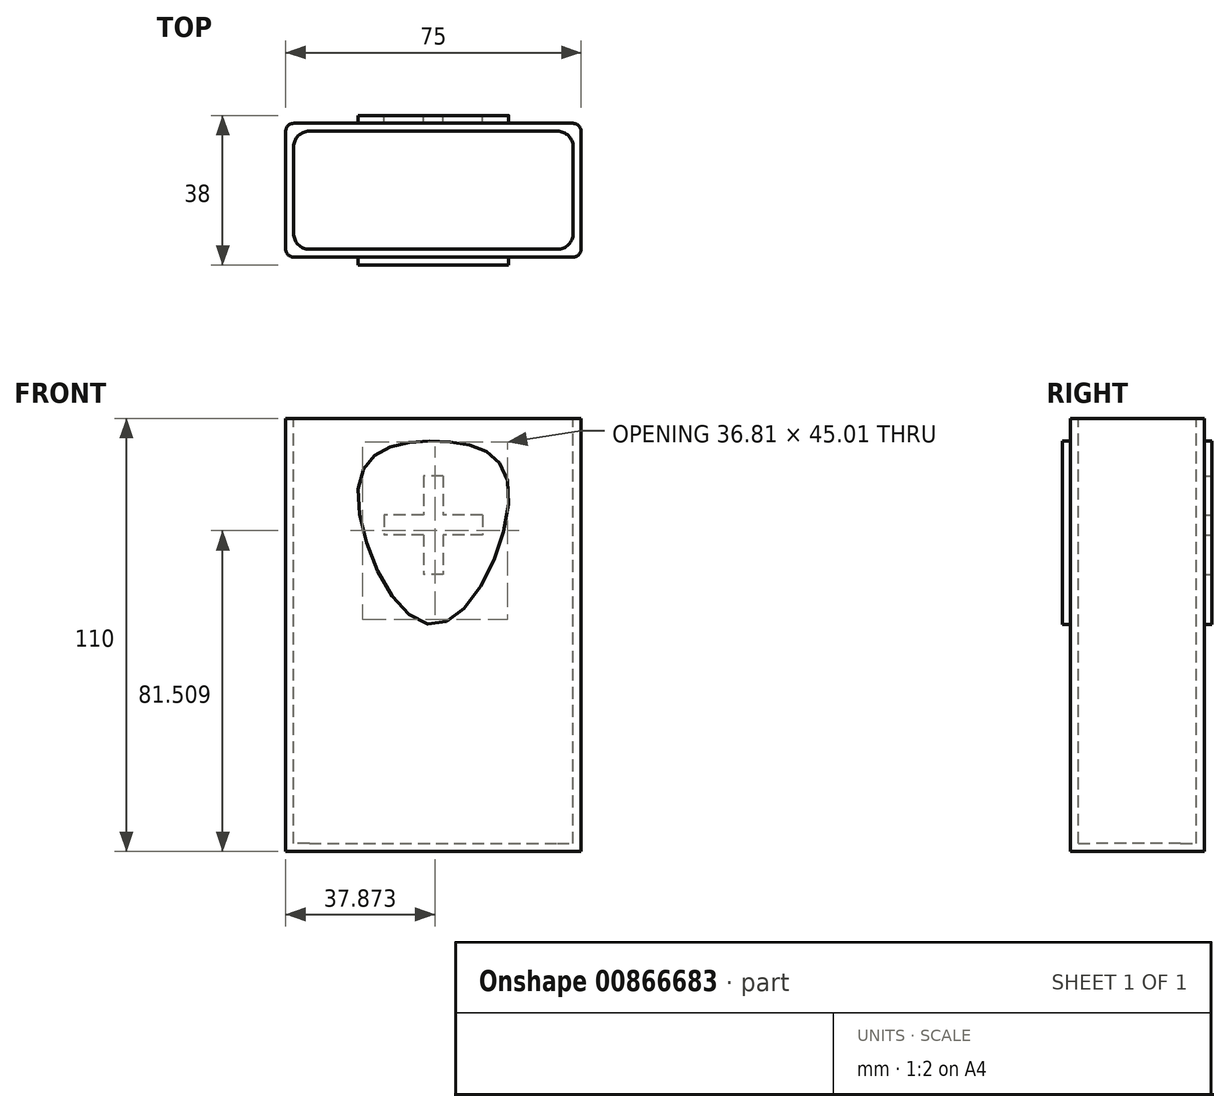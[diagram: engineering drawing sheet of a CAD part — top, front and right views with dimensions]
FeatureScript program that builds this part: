
annotation { "Feature Type Name" : "Feature", "Feature Type Description" : "" }
export const myFeature = defineFeature(function(context is Context, id is Id, definition is map)
    precondition{}
    {
        {
            var Q0;
            Q0=qCreatedBy(makeId("Top.planeOp"),FACE);
            var sketch = newSketch(context, id + "F0", { "sketchPlane" : qUnion([Q0])});
            skLineSegment(sketch, "E0.bottom", {"start": v(-37.5, 17) * mm, "end": v(37.5, 17) * mm});
            skLineSegment(sketch, "E0.top", {"start": v(-37.5, -17) * mm, "end": v(37.5, -17) * mm});
            skLineSegment(sketch, "E0.left", {"start": v(-37.5, 17) * mm, "end": v(-37.5, -17) * mm});
            skLineSegment(sketch, "E0.right", {"start": v(37.5, 17) * mm, "end": v(37.5, -17) * mm});
            skPoint(sketch, "E0.middle", {"position": v(0, 0) * mm});
            skSolve(sketch);
        }
        {
            assignVariable(context, id + "F1", {"name" : "epaisseur", "anyValue" : 2});
        }
        {
            var Q0;
            Q0=makeQuery(id+"F0.imprint","IMPRINT",FACE,{"disambiguationData":[TD([[makeQuery(id+"F0.imprint","IMPRINT",EDGE,{"derivedFrom":sQuery(id+"F0.wireOp",EDGE,"E0.bottom")}),-1.0]])]});
            extrude(context, id + "F2", {"entities" : qUnion([Q0]), "depth" : 110 * mm, "offsetDistance" : 25 * mm});
        }
        {
            var Q0;
            Q0=makeQuery(id+"F2.opExtrude","CAP_FACE",FACE,{"disambiguationData":[OSD([sQuery(id+"F0.wireOp",EDGE,"E0.bottom"),sQuery(id+"F0.wireOp",EDGE,"E0.top"),sQuery(id+"F0.wireOp",EDGE,"E0.left"),sQuery(id+"F0.wireOp",EDGE,"E0.right")])],"isStart":false});
            var sketch = newSketch(context, id + "F3", { "sketchPlane" : qUnion([Q0])});
            skLineSegment(sketch, "E1.bottom", {"start": v(-35.5, 15) * mm, "end": v(35.5, 15) * mm});
            skLineSegment(sketch, "E1.top", {"start": v(-35.5, -15) * mm, "end": v(35.5, -15) * mm});
            skLineSegment(sketch, "E1.left", {"start": v(-35.5, 15) * mm, "end": v(-35.5, -15) * mm});
            skLineSegment(sketch, "E1.right", {"start": v(35.5, 15) * mm, "end": v(35.5, -15) * mm});
            skPoint(sketch, "E1.middle", {"position": v(0, 0) * mm});
            skSolve(sketch);
        }
        {
            var Q0;
            Q0 = qSketchRegion(id + "F3", true);
            extrude(context, id + "F4", {"entities" : qUnion([Q0]), "operationType" : NewBodyOperationType.REMOVE, "oppositeDirection" : true, "depth" : (110 - getVariable(context, 'epaisseur')) * mm, "offsetDistance" : 25 * mm});
        }
        {
            var Q0;
            Q0=makeQuery(id+"F2.opExtrude","SWEPT_EDGE",EDGE,{"disambiguationData":[OSD([sQuery(id+"F0.wireOp",EDGE,"E0.bottom"),sQuery(id+"F0.wireOp",EDGE,"E0.left")])]});
            var Q1;
            Q1=makeQuery(id+"F2.opExtrude","SWEPT_EDGE",EDGE,{"disambiguationData":[OSD([sQuery(id+"F0.wireOp",EDGE,"E0.bottom"),sQuery(id+"F0.wireOp",EDGE,"E0.right")])]});
            var Q2;
            Q2=makeQuery(id+"F2.opExtrude","SWEPT_EDGE",EDGE,{"disambiguationData":[OSD([sQuery(id+"F0.wireOp",EDGE,"E0.top"),sQuery(id+"F0.wireOp",EDGE,"E0.right")])]});
            var Q3;
            Q3=makeQuery(id+"F2.opExtrude","SWEPT_EDGE",EDGE,{"disambiguationData":[OSD([sQuery(id+"F0.wireOp",EDGE,"E0.top"),sQuery(id+"F0.wireOp",EDGE,"E0.left")])]});
            fillet(context, id + "F5", {"entities" : qUnion([Q0, Q1, Q2, Q3]), "radius" : 2 * mm, "tangentPropagation" : true, "allowEdgeOverflow" : false});
        }
        {
            var Q0;
            Q0=makeQuery(id+"F4.boolean.opBoolean","COPY",EDGE,{"derivedFrom":makeQuery(id+"F4.opExtrude","SWEPT_EDGE",EDGE,{"disambiguationData":[OSD([sQuery(id+"F3.wireOp",EDGE,"E1.bottom"),sQuery(id+"F3.wireOp",EDGE,"E1.left")])]})});
            var Q1;
            Q1=makeQuery(id+"F4.boolean.opBoolean","COPY",EDGE,{"derivedFrom":makeQuery(id+"F4.opExtrude","SWEPT_EDGE",EDGE,{"disambiguationData":[OSD([sQuery(id+"F3.wireOp",EDGE,"E1.top"),sQuery(id+"F3.wireOp",EDGE,"E1.left")])]})});
            var Q2;
            Q2=makeQuery(id+"F4.boolean.opBoolean","COPY",EDGE,{"derivedFrom":makeQuery(id+"F4.opExtrude","SWEPT_EDGE",EDGE,{"disambiguationData":[OSD([sQuery(id+"F3.wireOp",EDGE,"E1.bottom"),sQuery(id+"F3.wireOp",EDGE,"E1.right")])]})});
            var Q3;
            Q3=makeQuery(id+"F4.boolean.opBoolean","COPY",EDGE,{"derivedFrom":makeQuery(id+"F4.opExtrude","SWEPT_EDGE",EDGE,{"disambiguationData":[OSD([sQuery(id+"F3.wireOp",EDGE,"E1.top"),sQuery(id+"F3.wireOp",EDGE,"E1.right")])]})});
            fillet(context, id + "F6", {"entities" : qUnion([Q0, Q1, Q2, Q3]), "radius" : 4 * mm, "tangentPropagation" : true, "allowEdgeOverflow" : false});
        }
        {
            var Q0;
            Q0=makeQuery(id+"F2.opExtrude","SWEPT_FACE",FACE,{"disambiguationData":[OSD([sQuery(id+"F0.wireOp",EDGE,"E0.top")])]});
            var sketch = newSketch(context, id + "F7", { "sketchPlane" : qUnion([Q0])});
            skLineSegment(sketch, "E2", {"start": v(0, 94.3) * mm, "end": v(18.78, 94.3) * mm, "construction": true});
            skLineSegment(sketch, "E3", {"start": v(18.78, 94.3) * mm, "end": v(0, 57.62) * mm, "construction": true});
            skLineSegment(sketch, "E4", {"start": v(0, 57.62) * mm, "end": v(0, 94.3) * mm, "construction": true});
            skLineSegment(sketch, "E5.MirrorCS", {"start": v(0, 94.3) * mm, "end": v(-18.78, 94.3) * mm, "construction": true});
            skLineSegment(sketch, "E6.MirrorCS", {"start": v(-18.78, 94.3) * mm, "end": v(0, 57.62) * mm, "construction": true});
            skPoint(sketch, "E7.1.internal.snap0", {"position": v(0, 110) * mm});
            skFitSpline(sketch, "E7", {"points": [v(18.78, 94.3) * mm, v(0, 104.23) * mm, v(-18.78, 94.3) * mm, v(0, 57.62) * mm, v(18.78, 94.3) * mm]});
            skSolve(sketch);
        }
        {
            var Q0;
            Q0=makeQuery(id+"F7.imprint","IMPRINT",FACE,{"disambiguationData":[TD([[makeQuery(id+"F7.imprint","IMPRINT",EDGE,{"derivedFrom":sQuery(id+"F7.wireOp",EDGE,"E7")}),1.0]])]});
            extrude(context, id + "F8", {"entities" : qUnion([Q0]), "operationType" : NewBodyOperationType.ADD, "depth" : 2 * mm, "offsetDistance" : 25 * mm});
        }
        {
            var Q0;
            Q0=makeQuery(id+"F2.opExtrude","SWEPT_BODY",BODY,{"disambiguationData":[OSD([sQuery(id+"F0.wireOp",EDGE,"E0.bottom"),sQuery(id+"F0.wireOp",EDGE,"E0.top"),sQuery(id+"F0.wireOp",EDGE,"E0.left"),sQuery(id+"F0.wireOp",EDGE,"E0.right")])]});
            var Q1;
            Q1=qCreatedBy(makeId("Front.planeOp"),FACE);
            mirror(context, id + "F9", {"operationType" : NewBodyOperationType.ADD, "entities" : qUnion([Q0]), "mirrorPlane" : qUnion([Q1])});
        }
        {
            var Q0;
            Q0=makeQuery(id+"F9.opPattern","COPY",FACE,{"derivedFrom":makeQuery(id+"F8.opExtrude","CAP_FACE",FACE,{"disambiguationData":[OSD([sQuery(id+"F7.wireOp",EDGE,"E7")])],"isStart":false}),"instanceName":"1"});
            var sketch = newSketch(context, id + "F10", { "sketchPlane" : qUnion([Q0])});
            skLineSegment(sketch, "E8", {"start": v(0, 57.62) * mm, "end": v(0, 104.23) * mm, "construction": true});
            skLineSegment(sketch, "E9", {"start": v(-18.23, 82.93) * mm, "end": v(18.23, 82.93) * mm, "construction": true});
            skLineSegment(sketch, "E10.bottom", {"start": v(-12.5, 85.43) * mm, "end": v(12.5, 85.43) * mm});
            skLineSegment(sketch, "E10.top", {"start": v(-12.5, 80.43) * mm, "end": v(12.5, 80.43) * mm});
            skLineSegment(sketch, "E10.left", {"start": v(-12.5, 85.43) * mm, "end": v(-12.5, 80.43) * mm});
            skLineSegment(sketch, "E10.right", {"start": v(12.5, 85.43) * mm, "end": v(12.5, 80.43) * mm});
            skPoint(sketch, "E10.middle", {"position": v(0, 82.93) * mm});
            skLineSegment(sketch, "E11.bottom", {"start": v(-2.5, 95.43) * mm, "end": v(2.5, 95.43) * mm});
            skLineSegment(sketch, "E11.top", {"start": v(-2.5, 70.43) * mm, "end": v(2.5, 70.43) * mm});
            skLineSegment(sketch, "E11.left", {"start": v(-2.5, 95.43) * mm, "end": v(-2.5, 70.43) * mm});
            skLineSegment(sketch, "E11.right", {"start": v(2.5, 95.43) * mm, "end": v(2.5, 70.43) * mm});
            skSolve(sketch);
        }
        {
            var Q0;
            {var subQ5=sQuery(id+"F10.wireOp",EDGE,"E11.bottom");Q0=makeQuery(id+"F10.imprint","IMPRINT",FACE,{"disambiguationData":[TD([[makeQuery(id+"F10.imprint","IMPRINT",EDGE,{"derivedFrom":subQ5}),-1.0]])]});}
            var Q1;
            {var subQ0=sQuery(id+"F10.wireOp",EDGE,"E10.left");Q1=makeQuery(id+"F10.imprint","IMPRINT",FACE,{"disambiguationData":[TD([[makeQuery(id+"F10.imprint","IMPRINT",EDGE,{"derivedFrom":subQ0}),1.0]])]});}
            var Q2;
            {var subQ0=sQuery(id+"F10.wireOp",EDGE,"E11.left");var subQ1=sQuery(id+"F10.wireOp",EDGE,"E10.bottom");var subQ2=makeQuery(id+"F10.imprint","INTERSECT",VERTEX,{"derivedFrom":[subQ1,subQ0]});Q2=makeQuery(id+"F10.imprint","IMPRINT",FACE,{"disambiguationData":[TD([[makeQuery(id+"F10.imprint","IMPRINT",EDGE,{"disambiguationData":[TD([[subQ2,-1.0]])],"derivedFrom":subQ1}),-1.0]])]});}
            var Q3;
            {var subQ0=sQuery(id+"F10.wireOp",EDGE,"E10.right");Q3=makeQuery(id+"F10.imprint","IMPRINT",FACE,{"disambiguationData":[TD([[makeQuery(id+"F10.imprint","IMPRINT",EDGE,{"derivedFrom":subQ0}),-1.0]])]});}
            var Q4;
            {var subQ5=sQuery(id+"F10.wireOp",EDGE,"E11.top");Q4=makeQuery(id+"F10.imprint","IMPRINT",FACE,{"disambiguationData":[TD([[makeQuery(id+"F10.imprint","IMPRINT",EDGE,{"derivedFrom":subQ5}),1.0]])]});}
            extrude(context, id + "F11", {"entities" : qUnion([Q0, Q1, Q2, Q3, Q4]), "operationType" : NewBodyOperationType.REMOVE, "oppositeDirection" : true, "depth" : 2 * mm, "offsetDistance" : 25 * mm});
        }
    });
